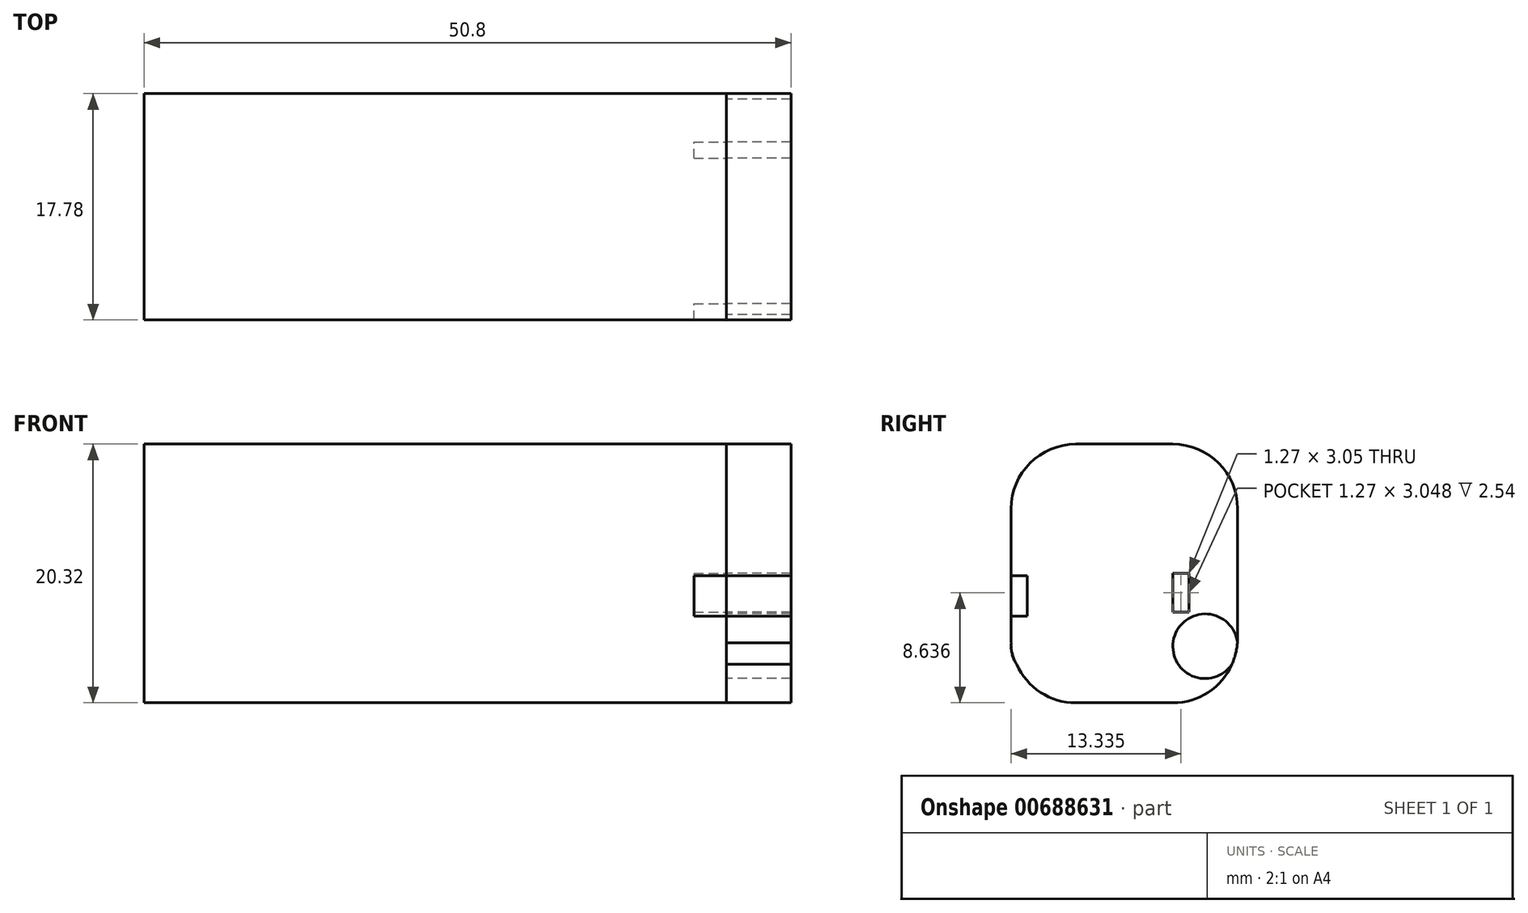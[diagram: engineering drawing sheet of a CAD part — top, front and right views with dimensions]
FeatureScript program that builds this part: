
annotation { "Feature Type Name" : "Feature", "Feature Type Description" : "" }
export const myFeature = defineFeature(function(context is Context, id is Id, definition is map)
    precondition{}
    {
        {
            var Q0;
            Q0=qCreatedBy(makeId("Top.planeOp"),FACE);
            var sketch = newSketch(context, id + "F0", { "sketchPlane" : qUnion([Q0])});
            skLineSegment(sketch, "E0.bottom", {"start": v(0, 0) * mm, "end": v(45.72, 0) * mm});
            skLineSegment(sketch, "E0.top", {"start": v(0, 17.78) * mm, "end": v(45.72, 17.78) * mm});
            skLineSegment(sketch, "E0.left", {"start": v(0, 0) * mm, "end": v(0, 17.78) * mm});
            skLineSegment(sketch, "E0.right", {"start": v(45.72, 0) * mm, "end": v(45.72, 17.78) * mm});
            skSolve(sketch);
        }
        {
            var Q0;
            Q0=makeQuery(id+"F0.imprint","IMPRINT",FACE,{"disambiguationData":[TD([[makeQuery(id+"F0.imprint","IMPRINT",EDGE,{"derivedFrom":sQuery(id+"F0.wireOp",EDGE,"E0.bottom")}),1.0]])]});
            extrude(context, id + "F1", {"entities" : qUnion([Q0]), "depth" : 20.32 * mm, "offsetDistance" : 25.4 * mm});
        }
        {
            var Q0;
            Q0=makeQuery(id+"F1.opExtrude","CAP_EDGE",EDGE,{"disambiguationData":[OSD([sQuery(id+"F0.wireOp",EDGE,"E0.top")])],"isStart":false});
            var Q1;
            Q1=makeQuery(id+"F1.opExtrude","CAP_EDGE",EDGE,{"disambiguationData":[OSD([sQuery(id+"F0.wireOp",EDGE,"E0.bottom")])],"isStart":false});
            var Q2;
            Q2=makeQuery(id+"F1.opExtrude","CAP_EDGE",EDGE,{"disambiguationData":[OSD([sQuery(id+"F0.wireOp",EDGE,"E0.top")])],"isStart":true});
            var Q3;
            Q3=makeQuery(id+"F1.opExtrude","CAP_EDGE",EDGE,{"disambiguationData":[OSD([sQuery(id+"F0.wireOp",EDGE,"E0.bottom")])],"isStart":true});
            fillet(context, id + "F2", {"entities" : qUnion([Q0, Q1, Q2, Q3]), "radius" : 5.08 * mm, "tangentPropagation" : true, "allowEdgeOverflow" : false});
        }
        {
            var Q0;
            Q0=makeQuery(id+"F1.opExtrude","SWEPT_FACE",FACE,{"disambiguationData":[OSD([sQuery(id+"F0.wireOp",EDGE,"E0.right")])]});
            var sketch = newSketch(context, id + "F3", { "sketchPlane" : qUnion([Q0])});
            skPoint(sketch, "E1.oppositeSnap0", {"position": v(5.08, 12.07) * mm});
            skLineSegment(sketch, "E1.bottom", {"start": v(5.08, 12.07) * mm, "end": v(0, 12.07) * mm});
            skLineSegment(sketch, "E1.top", {"start": v(5.08, 12.07) * mm, "end": v(0, 12.07) * mm});
            skLineSegment(sketch, "E1.left", {"start": v(5.08, 12.07) * mm, "end": v(5.08, 12.07) * mm});
            skLineSegment(sketch, "E1.right", {"start": v(0, 12.07) * mm, "end": v(0, 12.07) * mm});
            skLineSegment(sketch, "E2.top", {"start": v(5.08, 6.99) * mm, "end": v(5.08, 6.99) * mm});
            skLineSegment(sketch, "E2.left", {"start": v(5.08, 12.07) * mm, "end": v(5.08, 6.99) * mm});
            skLineSegment(sketch, "E2.right", {"start": v(5.08, 12.07) * mm, "end": v(5.08, 6.99) * mm});
            skLineSegment(sketch, "E3", {"start": v(5.08, 6.99) * mm, "end": v(0, 6.99) * mm});
            skLineSegment(sketch, "E4", {"start": v(0, 6.99) * mm, "end": v(0, 12.07) * mm});
            skLineSegment(sketch, "E5", {"start": v(1.3, 12.07) * mm, "end": v(1.3, 6.99) * mm});
            skLineSegment(sketch, "E6", {"start": v(19.05, 12.07) * mm, "end": v(24.13, 12.07) * mm});
            skLineSegment(sketch, "E7", {"start": v(24.13, 12.07) * mm, "end": v(24.13, 6.99) * mm});
            skLineSegment(sketch, "E8", {"start": v(24.13, 6.99) * mm, "end": v(19.05, 6.99) * mm});
            skLineSegment(sketch, "E9", {"start": v(19.05, 6.99) * mm, "end": v(19.05, 12.07) * mm});
            skLineSegment(sketch, "E10", {"start": v(20.36, 12.07) * mm, "end": v(20.36, 6.99) * mm});
            skSolve(sketch);
        }
        {
            var Q0;
            {var subQ0=sQuery(id+"F3.wireOp",EDGE,"E2.right");Q0=makeQuery(id+"F3.imprint","IMPRINT",FACE,{"disambiguationData":[TD([[makeQuery(id+"F3.imprint","IMPRINT",EDGE,{"derivedFrom":subQ0}),-1.0]])]});}
            var Q1;
            {var subQ0=sQuery(id+"F3.wireOp",EDGE,"E7");Q1=makeQuery(id+"F3.imprint","IMPRINT",FACE,{"disambiguationData":[TD([[makeQuery(id+"F3.imprint","IMPRINT",EDGE,{"derivedFrom":subQ0}),-1.0]])]});}
            extrude(context, id + "F4", {"entities" : qUnion([Q0, Q1]), "operationType" : NewBodyOperationType.REMOVE, "oppositeDirection" : true, "depth" : 5.08 * mm, "offsetDistance" : 25.4 * mm});
        }
        {
            var Q0;
            Q0=makeQuery(id+"F1.opExtrude","SWEPT_FACE",FACE,{"disambiguationData":[OSD([sQuery(id+"F0.wireOp",EDGE,"E0.right")])]});
            var sketch = newSketch(context, id + "F5", { "sketchPlane" : qUnion([Q0])});
            skLineSegment(sketch, "E11.bottom", {"start": v(10.42, 10.16) * mm, "end": v(10.42, 10.16) * mm});
            skLineSegment(sketch, "E12", {"start": v(10.42, 10.16) * mm, "end": v(6.6, 7.62) * mm});
            skLineSegment(sketch, "E13", {"start": v(6.6, 7.62) * mm, "end": v(10.42, 5.08) * mm});
            skLineSegment(sketch, "E14", {"start": v(10.42, 5.08) * mm, "end": v(6.6, 2.54) * mm});
            skSolve(sketch);
        }
        {
            var Q0;
            Q0=sQuery(id+"F5.wireOp",EDGE,"E12");
            var Q1;
            Q1=sQuery(id+"F5.wireOp",EDGE,"E13");
            var Q2;
            Q2=sQuery(id+"F5.wireOp",EDGE,"E14");
            var Q3;
            Q3=sQuery(id+"F5.wireOp",EDGE,"A7QQq6rB-7oQf-CFzx-UfZA-0zDvD0Z0I7kP");
            extrude(context, id + "F6", {"bodyType" : ToolBodyType.SURFACE, "operationType" : NewBodyOperationType.REMOVE, "surfaceEntities" : qUnion([Q0, Q1, Q2, Q3]), "oppositeDirection" : true, "depth" : 1.27 * mm, "offsetDistance" : 25.4 * mm});
        }
        {
            var Q0;
            Q0=makeQuery(id+"F1.opExtrude","SWEPT_FACE",FACE,{"disambiguationData":[OSD([sQuery(id+"F0.wireOp",EDGE,"E0.right")])]});
            var sketch = newSketch(context, id + "F7", { "sketchPlane" : qUnion([Q0])});
            skLineSegment(sketch, "E15", {"start": v(5.08, 12.07) * mm, "end": v(12.7, 12.07) * mm});
            skSolve(sketch);
        }
        {
            var Q0;
            Q0=sQuery(id+"F7.wireOp",EDGE,"E15");
            extrude(context, id + "F8", {"bodyType" : ToolBodyType.SURFACE, "operationType" : NewBodyOperationType.REMOVE, "surfaceEntities" : qUnion([Q0]), "oppositeDirection" : true, "depth" : 1.27 * mm, "offsetDistance" : 25.4 * mm});
        }
        {
            var Q0;
            Q0=makeQuery(id+"F1.opExtrude","SWEPT_FACE",FACE,{"disambiguationData":[OSD([sQuery(id+"F0.wireOp",EDGE,"E0.right")])]});
            var sketch = newSketch(context, id + "F9", { "sketchPlane" : qUnion([Q0])});
            skLineSegment(sketch, "E16.bottom", {"start": v(12.7, 10.16) * mm, "end": v(13.97, 10.16) * mm});
            skLineSegment(sketch, "E16.top", {"start": v(12.7, 7.11) * mm, "end": v(13.97, 7.11) * mm});
            skLineSegment(sketch, "E16.left", {"start": v(12.7, 10.16) * mm, "end": v(12.7, 7.11) * mm});
            skLineSegment(sketch, "E16.right", {"start": v(13.97, 10.16) * mm, "end": v(13.97, 7.11) * mm});
            skLineSegment(sketch, "E17.bottom", {"start": v(0, 10) * mm, "end": v(1.27, 10) * mm});
            skLineSegment(sketch, "E17.top", {"start": v(0, 6.82) * mm, "end": v(1.27, 6.82) * mm});
            skLineSegment(sketch, "E17.left", {"start": v(0, 10) * mm, "end": v(0, 6.82) * mm});
            skLineSegment(sketch, "E17.right", {"start": v(1.27, 10) * mm, "end": v(1.27, 6.82) * mm});
            skSolve(sketch);
        }
        {
            var Q0;
            Q0=makeQuery(id+"F9.imprint","IMPRINT",FACE,{"disambiguationData":[TD([[makeQuery(id+"F9.imprint","IMPRINT",EDGE,{"derivedFrom":sQuery(id+"F9.wireOp",EDGE,"E17.bottom")}),-1.0]])]});
            var Q1;
            Q1=makeQuery(id+"F9.imprint","IMPRINT",FACE,{"disambiguationData":[TD([[makeQuery(id+"F9.imprint","IMPRINT",EDGE,{"derivedFrom":sQuery(id+"F9.wireOp",EDGE,"E16.bottom")}),-1.0]])]});
            extrude(context, id + "F10", {"entities" : qUnion([Q0, Q1]), "operationType" : NewBodyOperationType.REMOVE, "oppositeDirection" : true, "depth" : 2.54 * mm, "offsetDistance" : 25.4 * mm});
        }
        {
            var Q0;
            Q0=makeQuery(id+"F1.opExtrude","SWEPT_FACE",FACE,{"disambiguationData":[OSD([sQuery(id+"F0.wireOp",EDGE,"E0.right")])]});
            var sketch = newSketch(context, id + "F11", { "sketchPlane" : qUnion([Q0])});
            skCircle(sketch, "E18", {"center": v(2.54, 4.44) * mm, "radius": 2.54 * mm});
            skPoint(sketch, "E19.endSnap0", {"position": v(5.08, 12.7) * mm});
            skCircle(sketch, "E20.MirrorC", {"center": v(15.24, 4.44) * mm, "radius": 2.54 * mm});
            skSolve(sketch);
        }
        {
            var Q0;
            Q0=makeQuery(id+"F11.imprint","IMPRINT",FACE,{"disambiguationData":[TD([[makeQuery(id+"F11.imprint","IMPRINT",EDGE,{"derivedFrom":sQuery(id+"F11.wireOp",EDGE,"E18")}),1.0]])]});
            var Q1;
            Q1=makeQuery(id+"F11.imprint","IMPRINT",FACE,{"disambiguationData":[TD([[makeQuery(id+"F11.imprint","IMPRINT",EDGE,{"derivedFrom":sQuery(id+"F11.wireOp",EDGE,"E20.MirrorC")}),-1.0]])]});
            extrude(context, id + "F12", {"entities" : qUnion([Q0, Q1]), "depth" : 5.08 * mm, "offsetDistance" : 25.4 * mm});
        }
    });
